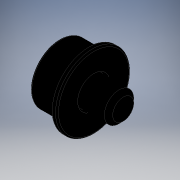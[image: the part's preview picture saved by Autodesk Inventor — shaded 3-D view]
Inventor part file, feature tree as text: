
AUTODESK INVENTOR PART (.ipt)
format: ipt  version: 2019 (Build 230136000, 136)  size: 200,192 bytes
history: native  units: mm
features: other x7, revolve x2, sketch x2
ambient origin geometry x8: Origin, YZ Plane, XZ Plane, XY Plane, X Axis, Y Axis, Z Axis, Center Point
bodies: Solid1 (feature_tree)
feature tree (11):
  revolve  "Revolution1"  Angle=360.0deg
  revolve  "Revolution2"  [1 undecoded]
  other  "to_block_XY"
  other  "to_block_YZ"
  other  "to_block_ZX"
  other  "to_block_X"
  other  "to_block_Y"
  other  "to_block_Z"
  other  "to_block_Center"
  sketch  "Sketch_1"  dims[d0=360.0deg d1=360.0deg]
  sketch  "Sketch_3"  dims[d2=0.0mm]
note: 1 required parameter value undecoded (feature->parameter linkage not recoverable at this tier; creation-order binding heuristic only, values carry confidence <= 0.55)
